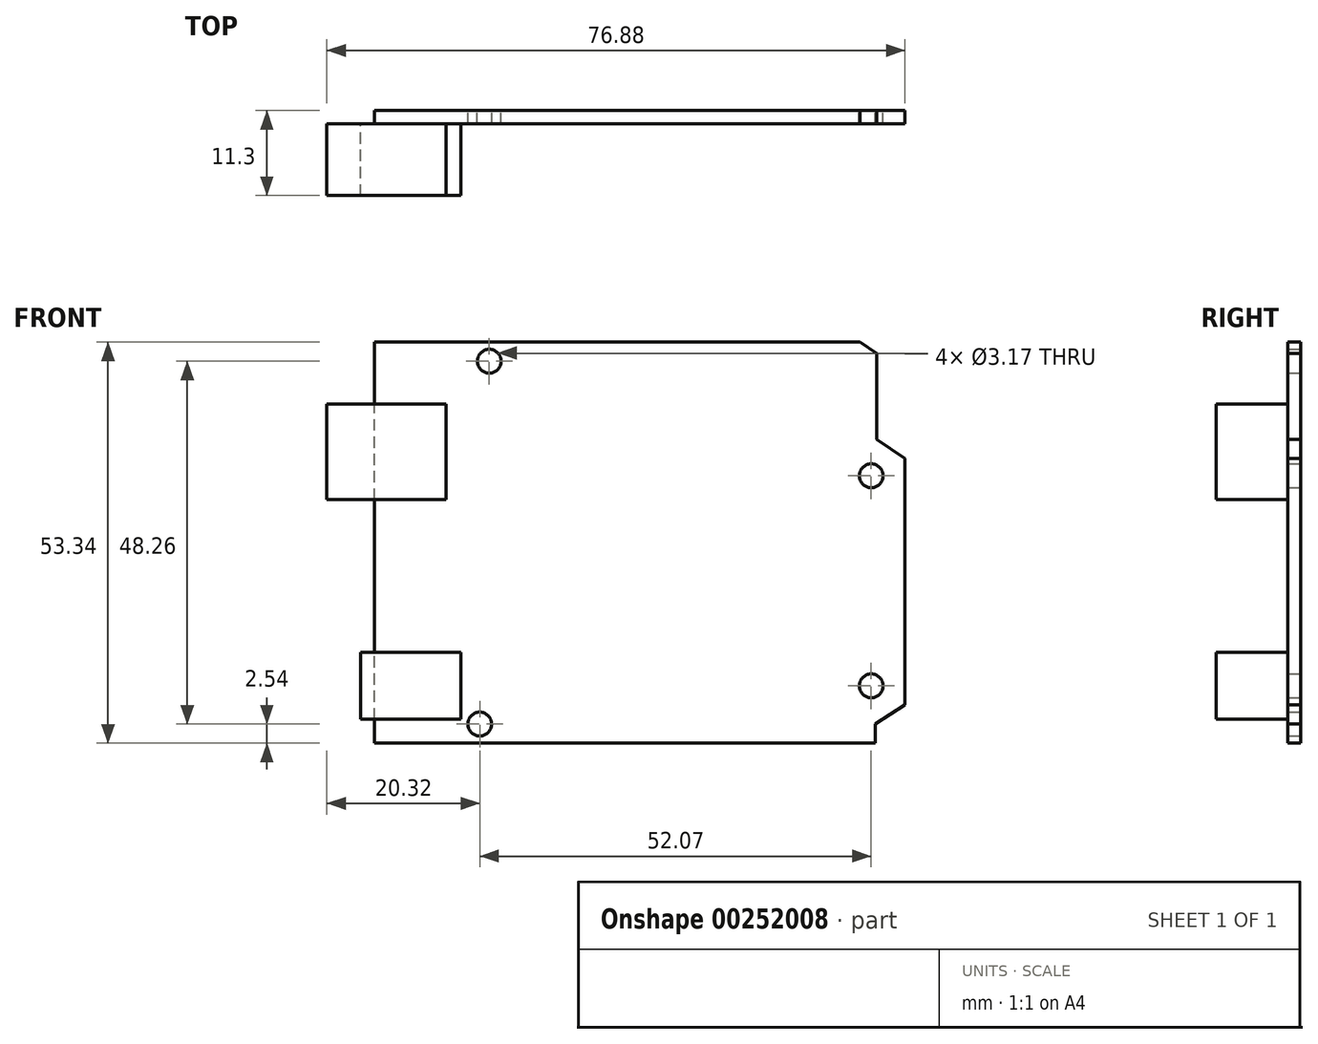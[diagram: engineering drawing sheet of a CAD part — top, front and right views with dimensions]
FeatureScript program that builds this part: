
annotation { "Feature Type Name" : "Feature", "Feature Type Description" : "" }
export const myFeature = defineFeature(function(context is Context, id is Id, definition is map)
    precondition{}
    {
        {
            var Q0;
            Q0=qCreatedBy(makeId("Front.planeOp"),FACE);
            var sketch = newSketch(context, id + "F0", { "sketchPlane" : qUnion([Q0])});
            skLineSegment(sketch, "E0", {"start": v(0, 0) * mm, "end": v(0, 53.34) * mm});
            skLineSegment(sketch, "E1", {"start": v(0, 53.34) * mm, "end": v(64.52, 53.34) * mm});
            skPoint(sketch, "E2", {"position": v(64.52, 53.34) * mm});
            skPoint(sketch, "E3", {"position": v(66.74, 51.82) * mm});
            skLineSegment(sketch, "E4", {"start": v(64.52, 53.34) * mm, "end": v(66.74, 51.82) * mm});
            skLineSegment(sketch, "E5", {"start": v(66.74, 51.82) * mm, "end": v(66.74, 40.39) * mm});
            skPoint(sketch, "E6", {"position": v(66.74, 40.39) * mm});
            skPoint(sketch, "E7", {"position": v(70.53, 37.85) * mm});
            skLineSegment(sketch, "E8", {"start": v(66.74, 40.39) * mm, "end": v(70.53, 37.85) * mm});
            skPoint(sketch, "E9", {"position": v(70.53, 5.08) * mm});
            skLineSegment(sketch, "E10", {"start": v(70.53, 37.85) * mm, "end": v(70.53, 5.08) * mm});
            skPoint(sketch, "E11", {"position": v(66.59, 2.54) * mm});
            skLineSegment(sketch, "E12", {"start": v(0, 0) * mm, "end": v(66.59, 0) * mm});
            skLineSegment(sketch, "E13", {"start": v(66.59, 0) * mm, "end": v(66.59, 2.54) * mm});
            skLineSegment(sketch, "E14", {"start": v(70.53, 5.08) * mm, "end": v(66.59, 2.54) * mm});
            skCircle(sketch, "E15", {"center": v(15.24, 50.8) * mm, "radius": 1.59 * mm});
            skCircle(sketch, "E16", {"center": v(13.97, 2.54) * mm, "radius": 1.59 * mm});
            skCircle(sketch, "E17", {"center": v(66.04, 35.56) * mm, "radius": 1.59 * mm});
            skCircle(sketch, "E18", {"center": v(66.04, 7.62) * mm, "radius": 1.59 * mm});
            skSolve(sketch);
        }
        {
            var Q0;
            Q0 = qSketchRegion(id + "F0", true);
            extrude(context, id + "F1", {"entities" : qUnion([Q0]), "depth" : 1.78 * mm});
        }
        {
            var Q0;
            Q0=makeQuery(id+"F1.opExtrude","CAP_FACE",FACE,{"disambiguationData":[OSD([sQuery(id+"F0.wireOp",EDGE,"E0"),sQuery(id+"F0.wireOp",EDGE,"E1"),sQuery(id+"F0.wireOp",EDGE,"E4"),sQuery(id+"F0.wireOp",EDGE,"E5"),sQuery(id+"F0.wireOp",EDGE,"E8"),sQuery(id+"F0.wireOp",EDGE,"E10"),sQuery(id+"F0.wireOp",EDGE,"E12"),sQuery(id+"F0.wireOp",EDGE,"E13"),sQuery(id+"F0.wireOp",EDGE,"E14"),sQuery(id+"F0.wireOp",EDGE,"E15"),sQuery(id+"F0.wireOp",EDGE,"E16"),sQuery(id+"F0.wireOp",EDGE,"E17"),sQuery(id+"F0.wireOp",EDGE,"E18")])],"isStart":false});
            var sketch = newSketch(context, id + "F2", { "sketchPlane" : qUnion([Q0])});
            skLineSegment(sketch, "E19.bottom", {"start": v(-1.9, 12.07) * mm, "end": v(11.43, 12.07) * mm});
            skLineSegment(sketch, "E19.top", {"start": v(-1.9, 3.18) * mm, "end": v(11.43, 3.18) * mm});
            skLineSegment(sketch, "E19.left", {"start": v(-1.9, 12.06) * mm, "end": v(-1.9, 3.17) * mm});
            skLineSegment(sketch, "E19.right", {"start": v(11.43, 12.07) * mm, "end": v(11.43, 3.18) * mm});
            skSolve(sketch);
        }
        {
            var Q0;
            Q0 = qSketchRegion(id + "F2", true);
            extrude(context, id + "F3", {"entities" : qUnion([Q0]), "operationType" : NewBodyOperationType.ADD, "depth" : 9.52 * mm});
        }
        {
            var Q0;
            Q0=makeQuery(id+"F1.opExtrude","CAP_FACE",FACE,{"disambiguationData":[OSD([sQuery(id+"F0.wireOp",EDGE,"E0"),sQuery(id+"F0.wireOp",EDGE,"E1"),sQuery(id+"F0.wireOp",EDGE,"E4"),sQuery(id+"F0.wireOp",EDGE,"E5"),sQuery(id+"F0.wireOp",EDGE,"E8"),sQuery(id+"F0.wireOp",EDGE,"E10"),sQuery(id+"F0.wireOp",EDGE,"E12"),sQuery(id+"F0.wireOp",EDGE,"E13"),sQuery(id+"F0.wireOp",EDGE,"E14"),sQuery(id+"F0.wireOp",EDGE,"E15"),sQuery(id+"F0.wireOp",EDGE,"E16"),sQuery(id+"F0.wireOp",EDGE,"E17"),sQuery(id+"F0.wireOp",EDGE,"E18")])],"isStart":false});
            var sketch = newSketch(context, id + "F4", { "sketchPlane" : qUnion([Q0])});
            skLineSegment(sketch, "E20.bottom", {"start": v(-6.35, 45.09) * mm, "end": v(9.52, 45.09) * mm});
            skLineSegment(sketch, "E20.top", {"start": v(-6.35, 32.39) * mm, "end": v(9.53, 32.39) * mm});
            skLineSegment(sketch, "E20.left", {"start": v(-6.35, 45.09) * mm, "end": v(-6.35, 32.39) * mm});
            skLineSegment(sketch, "E20.right", {"start": v(9.52, 45.09) * mm, "end": v(9.52, 32.39) * mm});
            skSolve(sketch);
        }
        {
            var Q0;
            Q0 = qSketchRegion(id + "F4", true);
            extrude(context, id + "F5", {"entities" : qUnion([Q0]), "operationType" : NewBodyOperationType.ADD, "depth" : 9.52 * mm});
        }
    });
